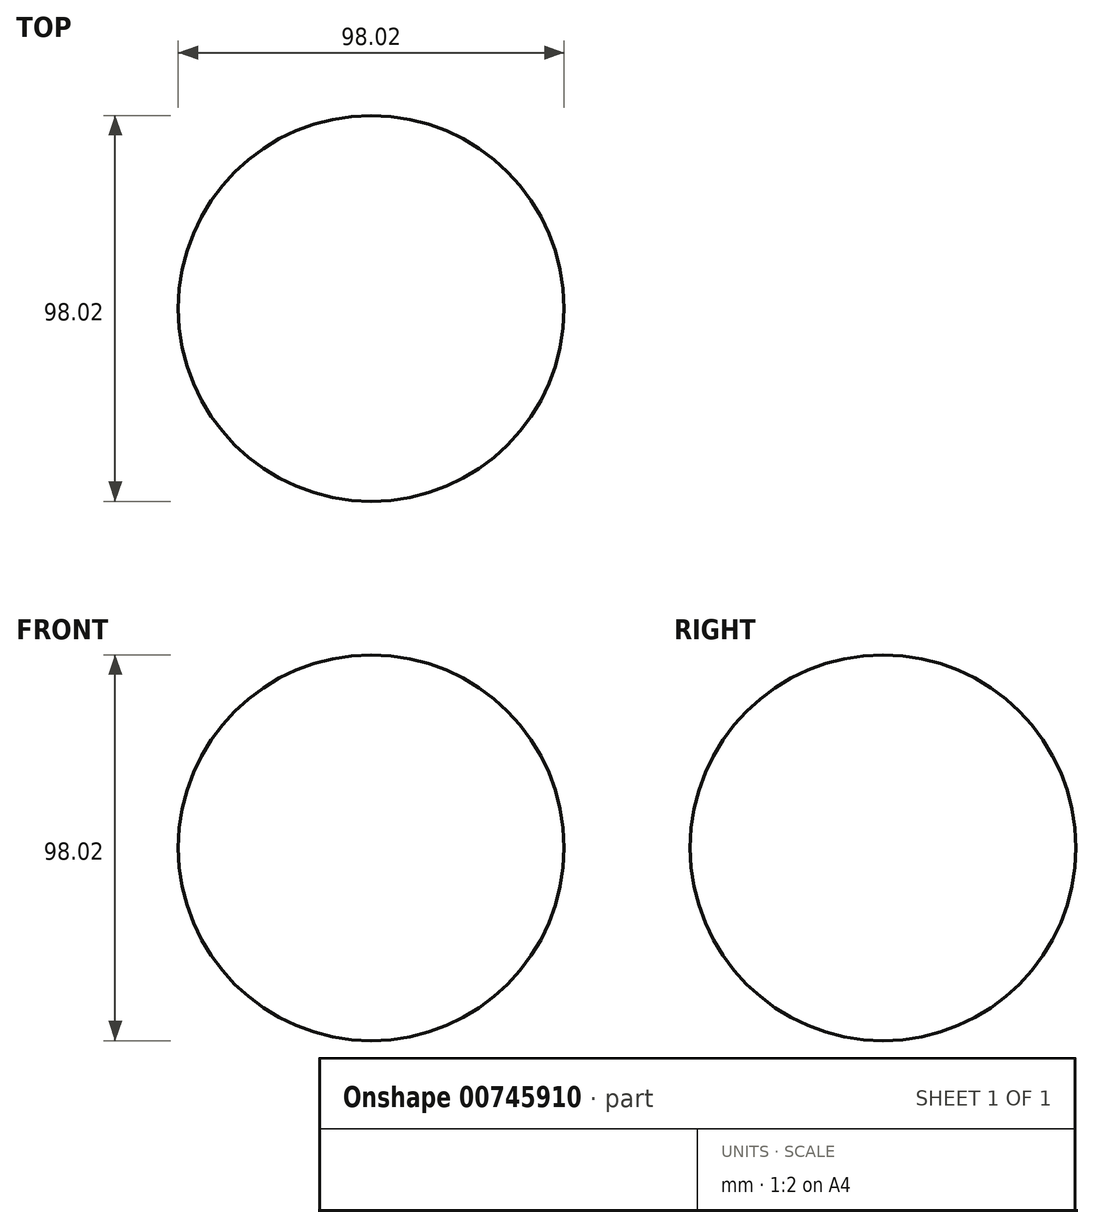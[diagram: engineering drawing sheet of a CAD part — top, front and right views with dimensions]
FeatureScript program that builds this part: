
annotation { "Feature Type Name" : "Feature", "Feature Type Description" : "" }
export const myFeature = defineFeature(function(context is Context, id is Id, definition is map)
    precondition{}
    {
        {
            var Q0;
            Q0=qCreatedBy(makeId("Front.planeOp"),FACE);
            var sketch = newSketch(context, id + "F0", { "sketchPlane" : qUnion([Q0])});
            skArc(sketch, "E0", {"start": v(49.01, 0) * mm, "mid": v(0, 49.01) * mm, "end": v(-49.01, 0) * mm});
            skLineSegment(sketch, "E1", {"start": v(-49.01, 0) * mm, "end": v(49.01, 0) * mm});
            skPoint(sketch, "E2.orphan", {"position": v(-55.76, 0) * mm});
            skSolve(sketch);
        }
        {
            var Q0;
            Q0=qSketchRegion(id+"F0",true);
            var Q1;
            Q1=sQuery(id+"F0.wireOp",EDGE,"E1");
            revolve(context, id + "F1", {"surfaceOperationType" : NewSurfaceOperationType.NEW, "entities" : qUnion([Q0]), "axis" : qUnion([Q1]), "revolveType" : RevolveType.FULL});
        }
    });
